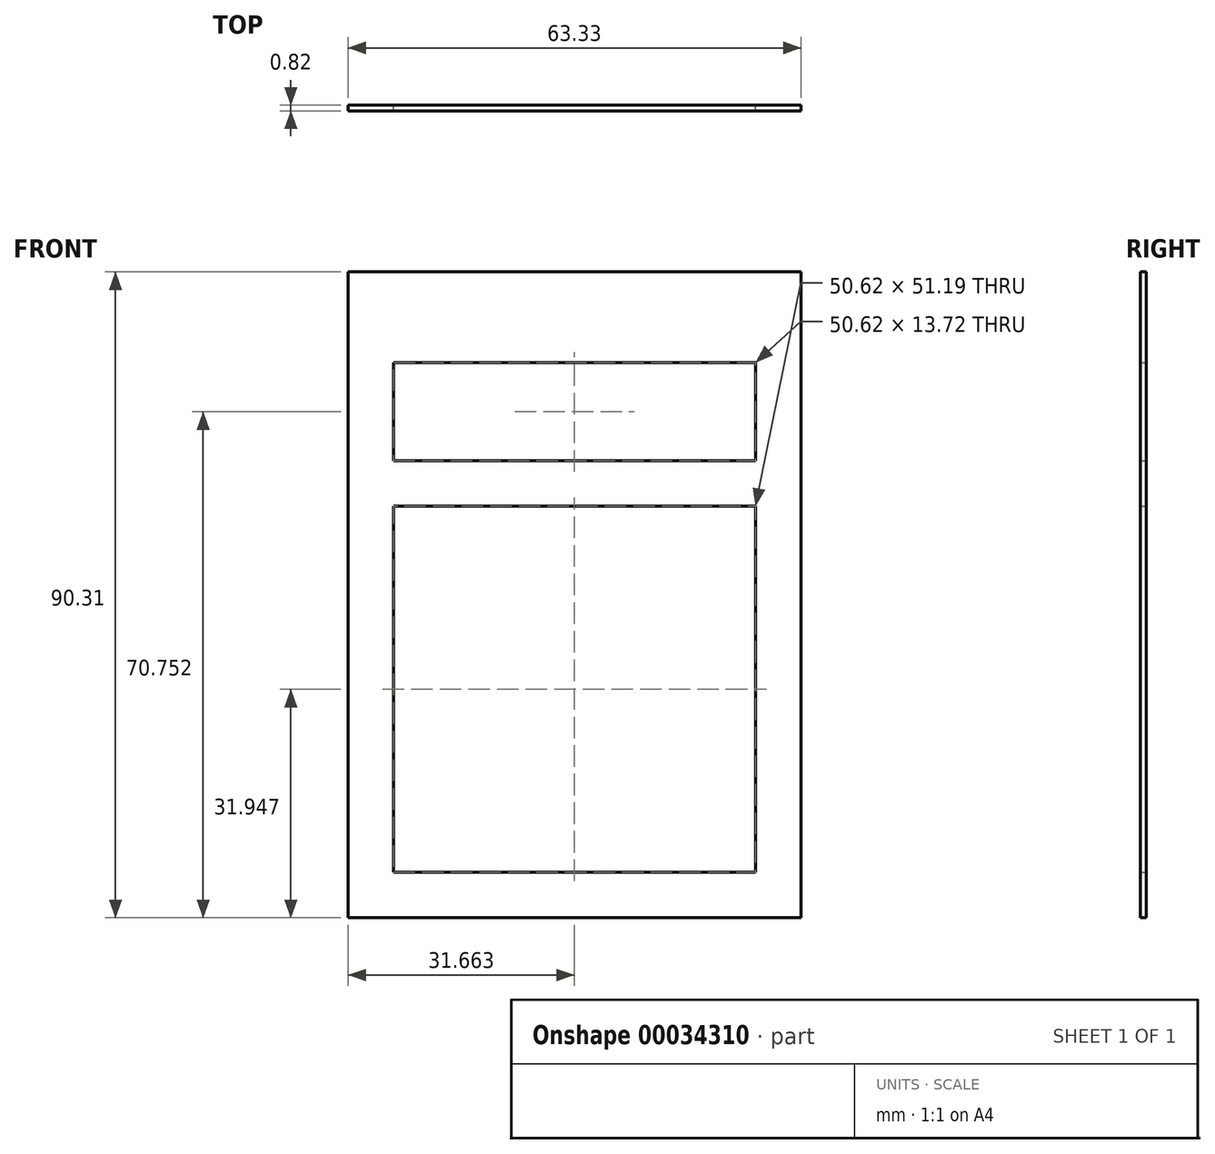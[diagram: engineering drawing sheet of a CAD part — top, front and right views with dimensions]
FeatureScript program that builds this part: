
annotation { "Feature Type Name" : "Feature", "Feature Type Description" : "" }
export const myFeature = defineFeature(function(context is Context, id is Id, definition is map)
    precondition{}
    {
        {
            var Q0;
            Q0=qCreatedBy(makeId("Front.planeOp"),FACE);
            var sketch = newSketch(context, id + "F0", { "sketchPlane" : qUnion([Q0])});
            skLineSegment(sketch, "E0", {"start": v(0, 0) * mm, "end": v(63.33, 0) * mm});
            skLineSegment(sketch, "E1", {"start": v(63.33, 0) * mm, "end": v(63.33, 90.31) * mm});
            skLineSegment(sketch, "E2", {"start": v(63.33, 90.31) * mm, "end": v(0, 90.3) * mm});
            skLineSegment(sketch, "E3", {"start": v(0, 90.3) * mm, "end": v(0, 0) * mm});
            skLineSegment(sketch, "E4", {"start": v(56.98, 0) * mm, "end": v(56.98, 6.35) * mm, "construction": true});
            skLineSegment(sketch, "E5", {"start": v(63.33, 6.37) * mm, "end": v(56.98, 6.35) * mm, "construction": true});
            skLineSegment(sketch, "E6", {"start": v(56.98, 6.35) * mm, "end": v(56.98, 6.35) * mm});
            skLineSegment(sketch, "E7", {"start": v(0, 0) * mm, "end": v(6.35, 0) * mm, "construction": true});
            skLineSegment(sketch, "E8", {"start": v(6.35, 0) * mm, "end": v(6.35, 6.35) * mm, "construction": true});
            skLineSegment(sketch, "E9", {"start": v(6.35, 6.35) * mm, "end": v(0, 6.35) * mm, "construction": true});
            skLineSegment(sketch, "E10", {"start": v(56.98, 6.35) * mm, "end": v(6.35, 6.35) * mm});
            skLineSegment(sketch, "E11", {"start": v(21.77, 57.54) * mm, "end": v(0, 57.54) * mm, "construction": true});
            skLineSegment(sketch, "E12", {"start": v(6.35, 6.35) * mm, "end": v(6.35, 57.54) * mm});
            skLineSegment(sketch, "E13", {"start": v(6.35, 57.54) * mm, "end": v(63.33, 57.54) * mm, "construction": true});
            skLineSegment(sketch, "E14", {"start": v(56.98, 6.35) * mm, "end": v(56.98, 57.54) * mm});
            skLineSegment(sketch, "E15", {"start": v(56.98, 57.54) * mm, "end": v(6.35, 57.54) * mm});
            skLineSegment(sketch, "E16", {"start": v(56.97, 90.31) * mm, "end": v(56.97, 83.96) * mm, "construction": true});
            skLineSegment(sketch, "E17", {"start": v(56.97, 83.96) * mm, "end": v(63.32, 83.96) * mm, "construction": true});
            skLineSegment(sketch, "E18", {"start": v(63.33, 57.54) * mm, "end": v(63.33, 57.54) * mm});
            skLineSegment(sketch, "E19", {"start": v(46.95, 57.54) * mm, "end": v(63.33, 57.54) * mm, "construction": true});
            skLineSegment(sketch, "E20", {"start": v(56.97, 83.96) * mm, "end": v(56.98, 57.54) * mm, "construction": true});
            skLineSegment(sketch, "E21", {"start": v(6.35, 57.54) * mm, "end": v(6.35, 83.96) * mm, "construction": true});
            skLineSegment(sketch, "E22", {"start": v(6.35, 83.96) * mm, "end": v(56.97, 83.96) * mm, "construction": true});
            skLineSegment(sketch, "E23", {"start": v(6.35, 83.96) * mm, "end": v(33.27, 83.96) * mm});
            skLineSegment(sketch, "E24", {"start": v(33.27, 83.96) * mm, "end": v(56.97, 83.96) * mm});
            skLineSegment(sketch, "E25", {"start": v(21.64, 63.9) * mm, "end": v(21.64, 57.54) * mm, "construction": true});
            skLineSegment(sketch, "E26", {"start": v(21.64, 63.9) * mm, "end": v(56.98, 63.9) * mm, "construction": true});
            skLineSegment(sketch, "E27", {"start": v(56.98, 63.9) * mm, "end": v(6.35, 63.9) * mm, "construction": true});
            skLineSegment(sketch, "E28", {"start": v(20.74, 83.96) * mm, "end": v(20.74, 77.61) * mm, "construction": true});
            skLineSegment(sketch, "E29", {"start": v(20.74, 77.61) * mm, "end": v(56.98, 77.61) * mm, "construction": true});
            skLineSegment(sketch, "E30", {"start": v(56.98, 77.61) * mm, "end": v(6.35, 77.61) * mm, "construction": true});
            skLineSegment(sketch, "E31", {"start": v(6.35, 77.61) * mm, "end": v(56.98, 77.61) * mm});
            skLineSegment(sketch, "E32", {"start": v(6.35, 77.61) * mm, "end": v(6.35, 63.9) * mm});
            skLineSegment(sketch, "E33", {"start": v(6.35, 63.9) * mm, "end": v(56.98, 63.9) * mm});
            skLineSegment(sketch, "E34", {"start": v(56.98, 77.61) * mm, "end": v(56.98, 63.9) * mm});
            skSolve(sketch);
        }
        {
            var Q0;
            Q0=makeQuery(id+"F0.imprint","IMPRINT",FACE,{"disambiguationData":[TD([[makeQuery(id+"F0.imprint","IMPRINT",EDGE,{"derivedFrom":sQuery(id+"F0.wireOp",EDGE,"E0")}),1.0]])]});
            extrude(context, id + "F1", {"entities" : qUnion([Q0]), "depth" : .82 * mm});
        }
    });
